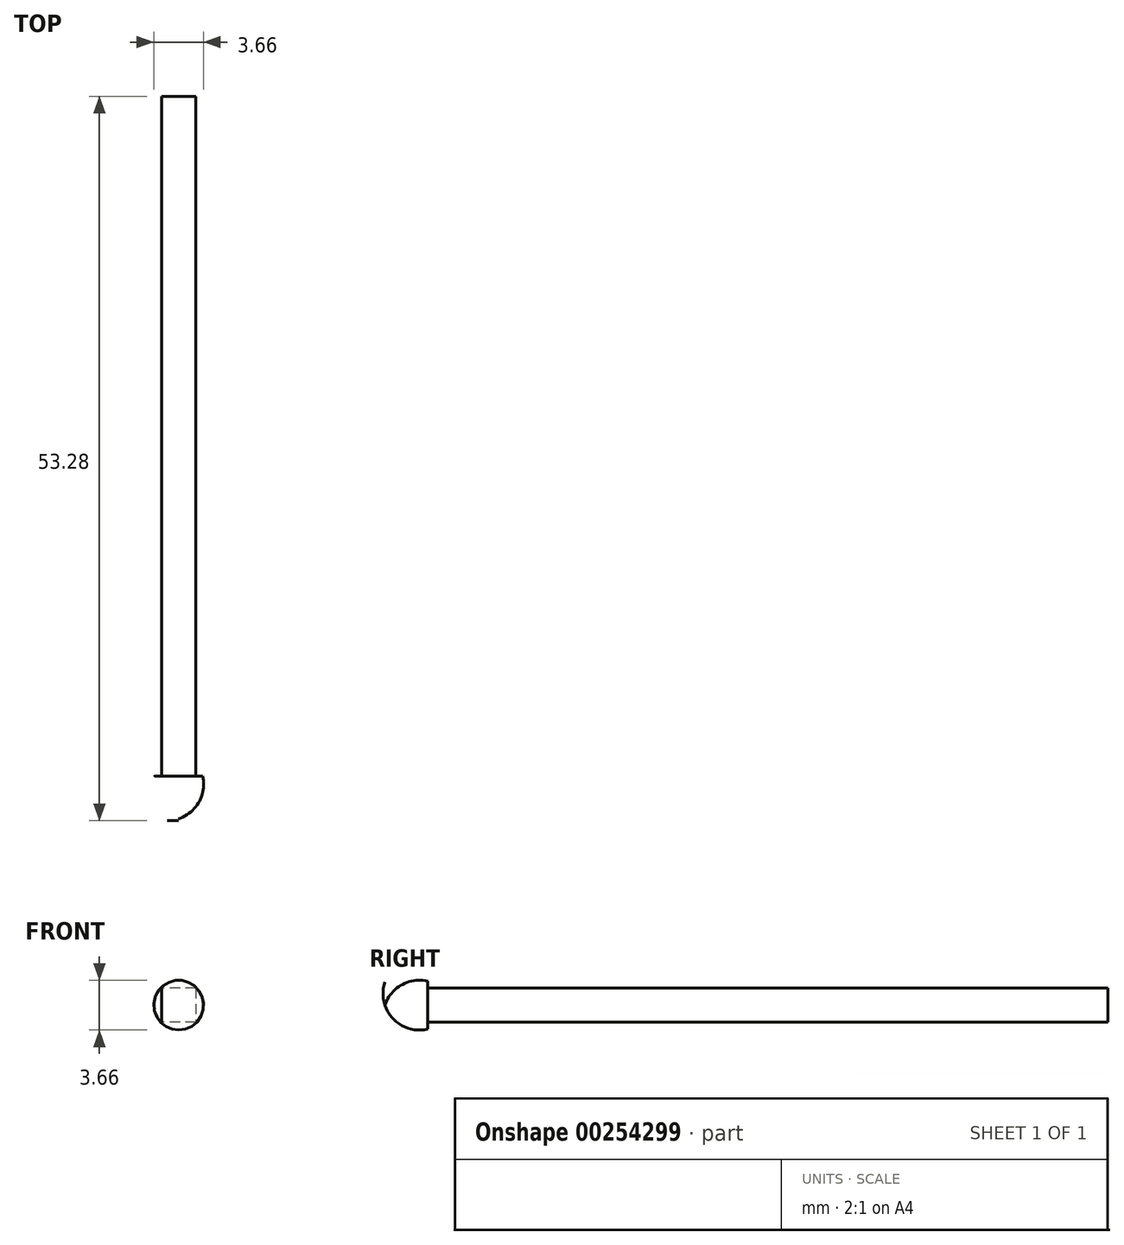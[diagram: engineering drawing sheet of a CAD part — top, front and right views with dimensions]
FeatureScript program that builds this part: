
annotation { "Feature Type Name" : "Feature", "Feature Type Description" : "" }
export const myFeature = defineFeature(function(context is Context, id is Id, definition is map)
    precondition{}
    {
        {
            var Q0;
            Q0=qCreatedBy(makeId("Front.planeOp"),FACE);
            var sketch = newSketch(context, id + "F0", { "sketchPlane" : qUnion([Q0])});
            skLineSegment(sketch, "E0.bottom", {"start": v(1.25, 1.25) * mm, "end": v(-1.25, 1.25) * mm});
            skLineSegment(sketch, "E0.top", {"start": v(1.25, -1.25) * mm, "end": v(-1.25, -1.25) * mm});
            skLineSegment(sketch, "E0.left", {"start": v(1.25, 1.25) * mm, "end": v(1.25, -1.25) * mm});
            skLineSegment(sketch, "E0.right", {"start": v(-1.25, 1.25) * mm, "end": v(-1.25, -1.25) * mm});
            skPoint(sketch, "E0.middle", {"position": v(0, 0) * mm});
            skSolve(sketch);
        }
        {
            var Q0;
            Q0=makeQuery(id+"F0.imprint","IMPRINT",FACE,{"disambiguationData":[TD([[makeQuery(id+"F0.imprint","IMPRINT",EDGE,{"derivedFrom":sQuery(id+"F0.wireOp",EDGE,"E0.bottom")}),1.0]])]});
            extrude(context, id + "F1", {"entities" : qUnion([Q0]), "depth" : 50 * mm});
        }
        {
            var Q0;
            Q0=makeQuery(id+"F1.opExtrude","CAP_FACE",FACE,{"disambiguationData":[OSD([sQuery(id+"F0.wireOp",EDGE,"E0.bottom"),sQuery(id+"F0.wireOp",EDGE,"E0.top"),sQuery(id+"F0.wireOp",EDGE,"E0.left"),sQuery(id+"F0.wireOp",EDGE,"E0.right")])],"isStart":false});
            var sketch = newSketch(context, id + "F2", { "sketchPlane" : qUnion([Q0])});
            skCircle(sketch, "E1", {"center": v(0, 0) * mm, "radius": 1.77 * mm});
            skSolve(sketch);
        }
        {
            var Q0;
            Q0=qCreatedBy(makeId("Top.planeOp"),FACE);
            var sketch = newSketch(context, id + "F3", { "sketchPlane" : qUnion([Q0])});
            skLineSegment(sketch, "E2.0", {"start": v(1.77, -50) * mm, "end": v(-1.77, -50) * mm});
            skLineSegment(sketch, "E3", {"start": v(0, -50) * mm, "end": v(0, -53.14) * mm});
            skPoint(sketch, "E3.endSnap0", {"position": v(0, -50) * mm});
            skArc(sketch, "E4", {"start": v(0, -53.14) * mm, "mid": v(1.49, -51.91) * mm, "end": v(1.77, -50) * mm});
            skSolve(sketch);
        }
        {
            var Q0;
            {var subQ2=sQuery(id+"F3.wireOp",EDGE,"E3");Q0=makeQuery(id+"F3.imprint","IMPRINT",FACE,{"disambiguationData":[TD([[makeQuery(id+"F3.imprint","IMPRINT",EDGE,{"derivedFrom":subQ2}),1.0]])]});}
            var Q1;
            Q1=sQuery(id+"F3.wireOp",EDGE,"E3");
            revolve(context, id + "F4", {"entities" : qUnion([Q0]), "axis" : qUnion([Q1]), "revolveType" : RevolveType.FULL});
        }
    });
